# Revit family: 3070 OXXIXXO
name_source: partatom
category: Doors
revit_build: Autodesk Revit 2018 (Build: 20170927_1515(x64)
units: mm (PartAtom-declared; Revit-internal decimal feet)

## family parameters
Always vertical = Yes
Cut with Voids When Loaded = No
Host = Wall
OmniClass Number = 23.30.10.00
OmniClass Title = Doors
Room Calculation Point = No
Shared = No

## types (1)
- 3070 OXXIXXO
    Actuator_Height = 48 "
    Bottom_Rail = 5.15 "
    Exterior_Head_Finish = 99.375 "
    Exterior_Head_Finish_Offset = 0.625 "
    Exterior_Wall_Finish_Location = 0.75 "
    Frame_&_Panel = Aluminum, Anodized Clear
    Frame_Head = 2.1523 "
    Frame_Jamb = 1.343 "
    Frame_Setback = 3.138 "
    Frame_Sill = 0.71 "
    Function = Interior
    Glazing = Glass
    Hardware_Finish = Stainless Steel, Brushed
    Height = 100 "
    Interior_Head_Finish = 99.375 "
    Interior_Head_Finish_Offset = 0.625 "
    Interior_Wall_Finish_Location = 0.5 "
    Interlock = 2.074 "
    L1_Panel_Width = 38.3139 "
    L2_Location = 36.9978 "
    L2_Panel_Width = 36.4189 "
    L3_Location = 71.3426 "
    L3_Panel_Width = 38.3139 "
    L4_Location = 71.3426 "
    L4_Panel_Width = 38.3139 "
    L5_Location = 36.9978 "
    L5_Panel_Width = 36.4189 "
    L6_Panel_Width = 38.3139 "
    Lead_Stile = 3.969 "
    Panel_Height = 98.4705 "
    Rough Height = 100.25 "
    Rough Width = 220.5 "
    Thickness = 5.724 "
    Top_Rail = 1.46 "
    Track_Width = 1.908 "
    Wall Closure = By host
    Width = 220 "

## geometry (parser evidence)
native form markers: Sweep x11
no freeform markers — native parametric forms only
